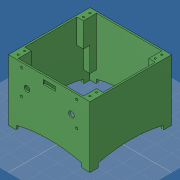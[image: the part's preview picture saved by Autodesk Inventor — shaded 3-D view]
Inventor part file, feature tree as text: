
AUTODESK INVENTOR PART (.ipt)
format: ipt  version: 2019 (Build 230136000, 136)  size: 208,896 bytes
history: native  units: mm
features: extrude x7, sketch x5, hole x1
ambient origin geometry x8: Origin, YZ Plane, XZ Plane, XY Plane, X Axis, Y Axis, Z Axis, Center Point
bodies: Volumenkörper1 (feature_tree)
feature tree (13):
  extrude  "Extrusion1"  Depth=100.0mm
  extrude  "Extrusion2"  Depth=5.0mm
  extrude  "Extrusion3"  Depth=50.0mm TaperAngle=0.0deg
  sketch  "Skizze9"  dims[d29=10.0mm d30=10.0mm d57=15.0mm d58=5.0mm d59=5.0mm d60=7.0mm d61=7.0mm d62=35.0mm d63=0.0mm d64=3.0mm d65=2.0mm d67=10.0mm d68=0.0mm d69=60.0mm d70=0.0mm d71=30.0mm d72=0.0mm d73=2.2mm d74=6.0mm d75=4.0mm d76=2.0mm d77=90.0deg d78=6.0mm d79=0.0mm d81=8.0mm d82=8.0mm]
  extrude  "Extrusion9"  Depth=50.0mm TaperAngle=0.0deg
  extrude  "Extrusion10"  Depth=10.0mm
  extrude  "Extrusion11"  Depth=15.0mm
  hole  "Bohrung3"  [1 undecoded]
  extrude  "Extrusion8"  Depth=5.0mm
  sketch  "Skizze1"  dims[d0=100.0mm d1=100.0mm]
  sketch  "Skizze2"  dims[d2=75.0mm d3=0.0mm d4=5.0mm]
  sketch  "Skizze3"  dims[d6=80.0mm d7=50.0mm d8=0.0mm]
  sketch  "Skizze8"  dims[d9=5.0mm d11=80.0mm d12=50.0mm d13=0.0mm]
note: 1 required parameter value undecoded (feature->parameter linkage not recoverable at this tier; creation-order binding heuristic only, values carry confidence <= 0.55)
